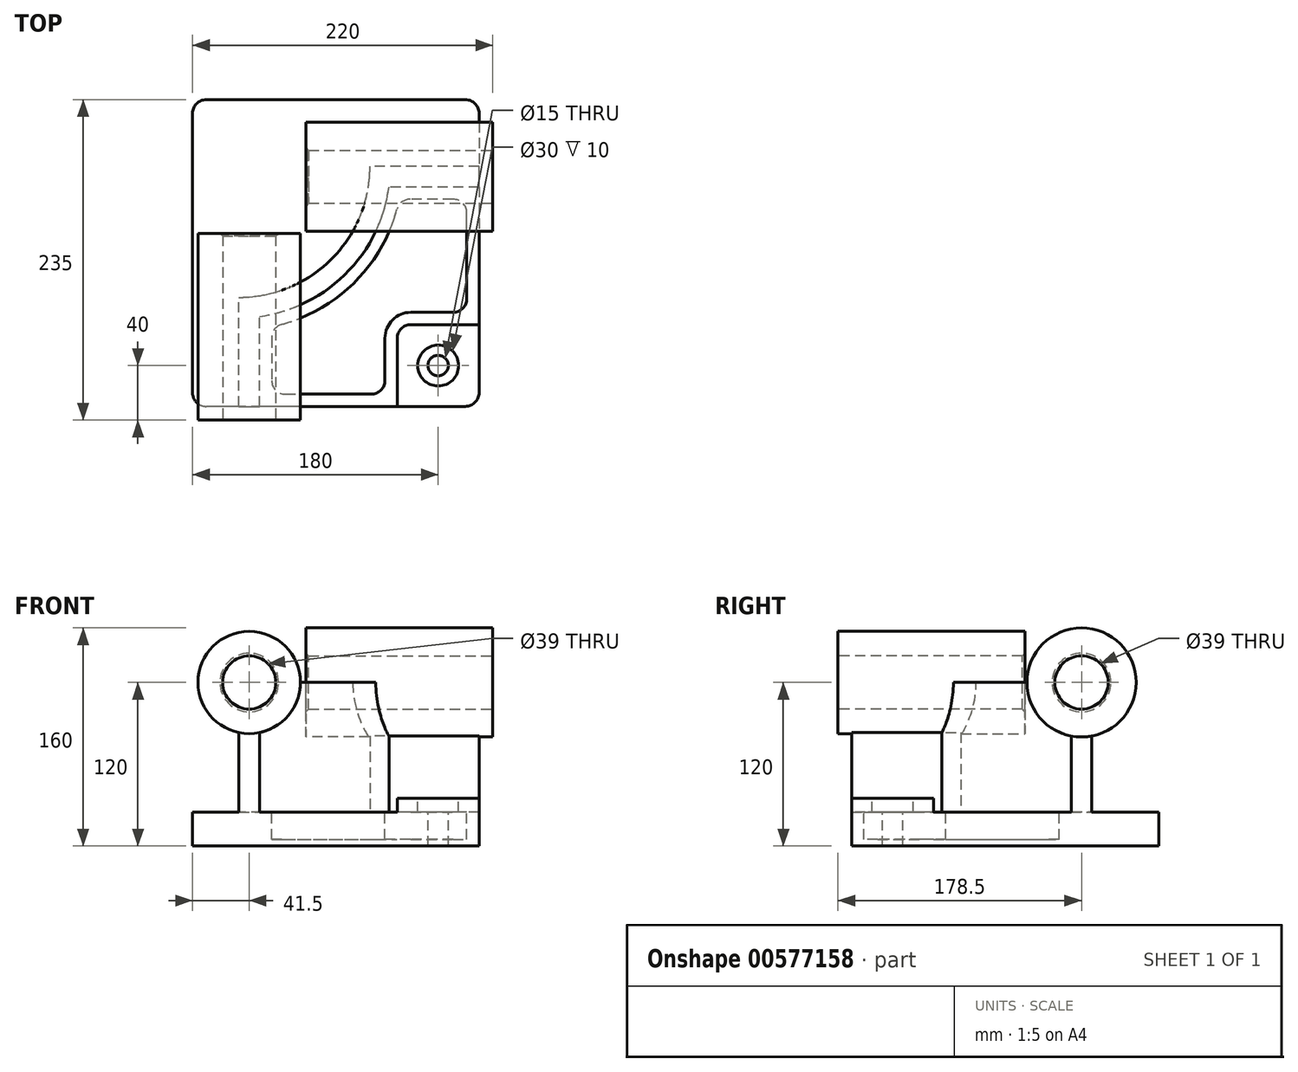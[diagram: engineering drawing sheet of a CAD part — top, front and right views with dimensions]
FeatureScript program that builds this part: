
annotation { "Feature Type Name" : "Feature", "Feature Type Description" : "" }
export const myFeature = defineFeature(function(context is Context, id is Id, definition is map)
    precondition{}
    {
        {
            var Q0;
            Q0=qCreatedBy(makeId("Top.planeOp"),FACE);
            var sketch = newSketch(context, id + "F0", { "sketchPlane" : qUnion([Q0])});
            skLineSegment(sketch, "E0.bottom", {"start": v(105, 112.5) * mm, "end": v(-105, 112.5) * mm});
            skLineSegment(sketch, "E0.top", {"start": v(105, -112.5) * mm, "end": v(-105, -112.5) * mm});
            skLineSegment(sketch, "E0.left", {"start": v(105, 112.5) * mm, "end": v(105, -112.5) * mm});
            skLineSegment(sketch, "E0.right", {"start": v(-105, 112.5) * mm, "end": v(-105, -112.5) * mm});
            skPoint(sketch, "E0.middle", {"position": v(0, 0) * mm});
            skSolve(sketch);
        }
        {
            var Q0;
            Q0=makeQuery(id+"F0.imprint","IMPRINT",FACE,{"disambiguationData":[TD([[makeQuery(id+"F0.imprint","IMPRINT",EDGE,{"derivedFrom":sQuery(id+"F0.wireOp",EDGE,"E0.bottom")}),1.0]])]});
            extrude(context, id + "F1", {"entities" : qUnion([Q0]), "depth" : 25 * mm, "offsetDistance" : 25 * mm});
        }
        {
            var Q0;
            Q0=makeQuery(id+"F1.opExtrude","CAP_FACE",FACE,{"disambiguationData":[OSD([sQuery(id+"F0.wireOp",EDGE,"E0.bottom"),sQuery(id+"F0.wireOp",EDGE,"E0.top"),sQuery(id+"F0.wireOp",EDGE,"E0.left"),sQuery(id+"F0.wireOp",EDGE,"E0.right")])],"isStart":false});
            var sketch = newSketch(context, id + "F2", { "sketchPlane" : qUnion([Q0])});
            skLineSegment(sketch, "E1", {"start": v(-71, -112.5) * mm, "end": v(-71, -32.5) * mm});
            skLineSegment(sketch, "E2", {"start": v(105, 63.5) * mm, "end": v(25, 63.5) * mm});
            skArc(sketch, "E3", {"start": v(-71, -32.5) * mm, "mid": v(-3.12, -4.38) * mm, "end": v(25, 63.5) * mm});
            skLineSegment(sketch, "E4", {"start": v(-71, 63.5) * mm, "end": v(25, 63.5) * mm, "construction": true});
            skLineSegment(sketch, "E5", {"start": v(-71, 63.5) * mm, "end": v(-71, -32.5) * mm, "construction": true});
            skLineSegment(sketch, "E6.0", {"start": v(-56, -112.5) * mm, "end": v(-56, -46.48) * mm});
            skArc(sketch, "E6.1", {"start": v(-56, -46.48) * mm, "mid": v(7.49, -14.99) * mm, "end": v(38.98, 48.5) * mm});
            skLineSegment(sketch, "E6.2", {"start": v(105, 48.5) * mm, "end": v(38.98, 48.5) * mm});
            skLineSegment(sketch, "E7.0", {"start": v(105, 112.5) * mm, "end": v(105, -112.5) * mm});
            skLineSegment(sketch, "E8.0", {"start": v(105, -112.5) * mm, "end": v(-105, -112.5) * mm});
            skSolve(sketch);
        }
        {
            var Q0;
            {var subQ2=sQuery(id+"F2.wireOp",EDGE,"E1");Q0=makeQuery(id+"F2.imprint","IMPRINT",FACE,{"disambiguationData":[TD([[makeQuery(id+"F2.imprint","IMPRINT",EDGE,{"derivedFrom":subQ2}),-1.0]])]});}
            extrude(context, id + "F3", {"entities" : qUnion([Q0]), "operationType" : NewBodyOperationType.ADD, "depth" : 95 * mm, "offsetDistance" : 25 * mm});
        }
        {
            var Q0;
            Q0=makeQuery(id+"F3.boolean.opBoolean","MERGE",FACE,{"derivedFrom":[makeQuery(id+"F1.opExtrude","SWEPT_FACE",FACE,{"disambiguationData":[OSD([sQuery(id+"F0.wireOp",EDGE,"E0.top")])]}),makeQuery(id+"F3.opExtrude","SWEPT_FACE",FACE,{"disambiguationData":[OSD([sQuery(id+"F2.wireOp",EDGE,"E8.0")])]})]});
            var sketch = newSketch(context, id + "F4", { "sketchPlane" : qUnion([Q0])});
            skCircle(sketch, "E9", {"center": v(-63.5, 120) * mm, "radius": 37.5 * mm});
            skSolve(sketch);
        }
        {
            var Q0;
            Q0 = qSketchRegion(id + "F4", true);
            extrude(context, id + "F5", {"entities" : qUnion([Q0]), "operationType" : NewBodyOperationType.ADD, "depth" : 10 * mm, "offsetDistance" : 25 * mm, "hasSecondDirection" : true, "secondDirectionOppositeDirection" : true, "secondDirectionDepth" : (137 - 10) * mm});
        }
        {
            var Q0;
            Q0=makeQuery(id+"F3.boolean.opBoolean","MERGE",FACE,{"derivedFrom":[makeQuery(id+"F1.opExtrude","SWEPT_FACE",FACE,{"disambiguationData":[OSD([sQuery(id+"F0.wireOp",EDGE,"E0.left")])]}),makeQuery(id+"F3.opExtrude","SWEPT_FACE",FACE,{"disambiguationData":[OSD([sQuery(id+"F2.wireOp",EDGE,"E7.0")])]})]});
            var sketch = newSketch(context, id + "F6", { "sketchPlane" : qUnion([Q0])});
            skCircle(sketch, "E10", {"center": v(56, 120) * mm, "radius": 40 * mm});
            skSolve(sketch);
        }
        {
            var Q0;
            Q0 = qSketchRegion(id + "F6", true);
            extrude(context, id + "F7", {"entities" : qUnion([Q0]), "operationType" : NewBodyOperationType.ADD, "depth" : 10 * mm, "offsetDistance" : 25 * mm, "hasSecondDirection" : true, "secondDirectionOppositeDirection" : true, "secondDirectionDepth" : (137 - 10) * mm});
        }
        {
            var Q0;
            {var subQ0=sQuery(id+"F0.wireOp",EDGE,"E0.left");var subQ1=sQuery(id+"F0.wireOp",EDGE,"E0.top");Q0=makeQuery(id+"F3.boolean.opBoolean","SPLIT",FACE,{"disambiguationData":[TD([makeQuery(id+"F3.opExtrude","SWEPT_FACE",FACE,{"disambiguationData":[OSD([sQuery(id+"F2.wireOp",EDGE,"E6.0")])]})])],"derivedFrom":makeQuery(id+"F1.opExtrude","CAP_FACE",FACE,{"disambiguationData":[OSD([sQuery(id+"F0.wireOp",EDGE,"E0.bottom"),subQ1,subQ0,sQuery(id+"F0.wireOp",EDGE,"E0.right")])],"isStart":false})});}
            var sketch = newSketch(context, id + "F8", { "sketchPlane" : qUnion([Q0])});
            skLineSegment(sketch, "E11.bottom", {"start": v(105, -112.5) * mm, "end": v(45, -112.5) * mm});
            skLineSegment(sketch, "E11.top", {"start": v(105, -52.5) * mm, "end": v(45, -52.5) * mm});
            skLineSegment(sketch, "E11.left", {"start": v(105, -112.5) * mm, "end": v(105, -52.5) * mm});
            skLineSegment(sketch, "E11.right", {"start": v(45, -112.5) * mm, "end": v(45, -52.5) * mm});
            skSolve(sketch);
        }
        {
            var Q0;
            Q0 = qSketchRegion(id + "F8", true);
            extrude(context, id + "F9", {"entities" : qUnion([Q0]), "operationType" : NewBodyOperationType.ADD, "depth" : (35 - 25) * mm, "offsetDistance" : 25 * mm});
        }
        {
            var Q0;
            Q0=makeQuery(id+"F9.opExtrude","SWEPT_EDGE",EDGE,{"disambiguationData":[OSD([sQuery(id+"F8.wireOp",EDGE,"E11.top"),sQuery(id+"F8.wireOp",EDGE,"E11.right")])]});
            fillet(context, id + "F10", {"entities" : qUnion([Q0]), "radius" : 10 * mm, "tangentPropagation" : true, "allowEdgeOverflow" : false});
        }
        {
            var Q0;
            {var subQ0=sQuery(id+"F0.wireOp",EDGE,"E0.left");var subQ1=sQuery(id+"F0.wireOp",EDGE,"E0.top");Q0=makeQuery(id+"F3.boolean.opBoolean","SPLIT",FACE,{"disambiguationData":[TD([makeQuery(id+"F3.opExtrude","SWEPT_FACE",FACE,{"disambiguationData":[OSD([sQuery(id+"F2.wireOp",EDGE,"E6.0")])]})])],"derivedFrom":makeQuery(id+"F1.opExtrude","CAP_FACE",FACE,{"disambiguationData":[OSD([sQuery(id+"F0.wireOp",EDGE,"E0.bottom"),subQ1,subQ0,sQuery(id+"F0.wireOp",EDGE,"E0.right")])],"isStart":false})});}
            var sketch = newSketch(context, id + "F11", { "sketchPlane" : qUnion([Q0])});
            skLineSegment(sketch, "E12.0", {"start": v(-47, -54.08) * mm, "end": v(-47, -103.5) * mm});
            skArc(sketch, "E12.1", {"start": v(46.58, 39.5) * mm, "mid": v(13.85, -21.35) * mm, "end": v(-47, -54.08) * mm});
            skLineSegment(sketch, "E12.2", {"start": v(-47, -103.5) * mm, "end": v(36, -103.5) * mm});
            skLineSegment(sketch, "E12.3", {"start": v(96, 39.5) * mm, "end": v(46.58, 39.5) * mm});
            skLineSegment(sketch, "E12.4", {"start": v(36, -103.5) * mm, "end": v(36, -62.5) * mm});
            skArc(sketch, "E12.5", {"start": v(36, -62.5) * mm, "mid": v(41.56, -49.06) * mm, "end": v(55, -43.5) * mm});
            skLineSegment(sketch, "E12.6", {"start": v(55, -43.5) * mm, "end": v(96, -43.5) * mm});
            skLineSegment(sketch, "E12.7", {"start": v(96, -43.5) * mm, "end": v(96, 39.5) * mm});
            skSolve(sketch);
        }
        {
            var Q0;
            Q0=makeQuery(id+"F11.imprint","IMPRINT",FACE,{"disambiguationData":[TD([[makeQuery(id+"F11.imprint","IMPRINT",EDGE,{"derivedFrom":sQuery(id+"F11.wireOp",EDGE,"E12.0")}),1.0]])]});
            extrude(context, id + "F12", {"entities" : qUnion([Q0]), "operationType" : NewBodyOperationType.REMOVE, "oppositeDirection" : true, "depth" : (25 - 5) * mm, "offsetDistance" : 25 * mm});
        }
        {
            var Q0;
            Q0=makeQuery(id+"F9.opExtrude","CAP_FACE",FACE,{"disambiguationData":[OSD([sQuery(id+"F8.wireOp",EDGE,"E11.bottom"),sQuery(id+"F8.wireOp",EDGE,"E11.top"),sQuery(id+"F8.wireOp",EDGE,"E11.left"),sQuery(id+"F8.wireOp",EDGE,"E11.right")])],"isStart":false});
            var sketch = newSketch(context, id + "F13", { "sketchPlane" : qUnion([Q0])});
            skCircle(sketch, "E13", {"center": v(75, -82.5) * mm, "radius": 15 * mm});
            skSolve(sketch);
        }
        {
            var Q0;
            Q0=sQuery(id+"F13.wireOp",VERTEX,"E13.center");
            var Q1;
            Q1=makeQuery(id+"F1.opExtrude","SWEPT_BODY",BODY,{"disambiguationData":[OSD([sQuery(id+"F0.wireOp",EDGE,"E0.bottom"),sQuery(id+"F0.wireOp",EDGE,"E0.top"),sQuery(id+"F0.wireOp",EDGE,"E0.left"),sQuery(id+"F0.wireOp",EDGE,"E0.right")])]});
            hole(context, id + "F14", {"style" : HoleStyle.C_BORE, "endStyle" : HoleEndStyle.THROUGH, "holeDiameter" : 15 * mm, "cBoreDiameter" : 30 * mm, "cBoreDepth" : 10 * mm, "isTappedThrough" : true, "tappedDepth" : 12 * mm, "tapClearance" : 3, "locations" : qUnion([Q0]), "scope" : qUnion([Q1])});
        }
        {
            var Q0;
            Q0=makeQuery(id+"F12.boolean.opBoolean","COPY",EDGE,{"derivedFrom":makeQuery(id+"F12.opExtrude","SWEPT_EDGE",EDGE,{"disambiguationData":[OSD([sQuery(id+"F11.wireOp",EDGE,"E12.0"),sQuery(id+"F11.wireOp",EDGE,"E12.1")])]})});
            var Q1;
            Q1=makeQuery(id+"F12.boolean.opBoolean","COPY",EDGE,{"derivedFrom":makeQuery(id+"F12.opExtrude","SWEPT_EDGE",EDGE,{"disambiguationData":[OSD([sQuery(id+"F11.wireOp",EDGE,"E12.1"),sQuery(id+"F11.wireOp",EDGE,"E12.3")])]})});
            var Q2;
            Q2=makeQuery(id+"F12.boolean.opBoolean","COPY",EDGE,{"derivedFrom":makeQuery(id+"F12.opExtrude","SWEPT_EDGE",EDGE,{"disambiguationData":[OSD([sQuery(id+"F11.wireOp",EDGE,"E12.0"),sQuery(id+"F11.wireOp",EDGE,"E12.2")])]})});
            var Q3;
            Q3=makeQuery(id+"F12.boolean.opBoolean","COPY",EDGE,{"derivedFrom":makeQuery(id+"F12.opExtrude","SWEPT_EDGE",EDGE,{"disambiguationData":[OSD([sQuery(id+"F11.wireOp",EDGE,"E12.3"),sQuery(id+"F11.wireOp",EDGE,"E12.7")])]})});
            var Q4;
            Q4=makeQuery(id+"F12.boolean.opBoolean","COPY",EDGE,{"derivedFrom":makeQuery(id+"F12.opExtrude","SWEPT_EDGE",EDGE,{"disambiguationData":[OSD([sQuery(id+"F11.wireOp",EDGE,"E12.2"),sQuery(id+"F11.wireOp",EDGE,"E12.4")])]})});
            var Q5;
            Q5=makeQuery(id+"F12.boolean.opBoolean","COPY",EDGE,{"derivedFrom":makeQuery(id+"F12.opExtrude","SWEPT_EDGE",EDGE,{"disambiguationData":[OSD([sQuery(id+"F11.wireOp",EDGE,"E12.6"),sQuery(id+"F11.wireOp",EDGE,"E12.7")])]})});
            fillet(context, id + "F15", {"entities" : qUnion([Q0, Q1, Q2, Q3, Q4, Q5]), "radius" : 10 * mm, "tangentPropagation" : true, "allowEdgeOverflow" : false});
        }
        {
            var Q0;
            Q0=makeQuery(id+"F5.opExtrude","CAP_FACE",FACE,{"disambiguationData":[OSD([sQuery(id+"F4.wireOp",EDGE,"E9")])],"isStart":false});
            var sketch = newSketch(context, id + "F16", { "sketchPlane" : qUnion([Q0])});
            skCircle(sketch, "E14", {"center": v(-63.5, 120) * mm, "radius": 19.5 * mm});
            skSolve(sketch);
        }
        {
            var Q0;
            Q0 = qSketchRegion(id + "F16", true);
            extrude(context, id + "F17", {"entities" : qUnion([Q0]), "operationType" : NewBodyOperationType.REMOVE, "endBound" : BoundingType.THROUGH_ALL, "oppositeDirection" : true, "depth" : 25 * mm, "offsetDistance" : 25 * mm});
        }
        {
            var Q0;
            Q0=makeQuery(id+"F7.opExtrude","CAP_FACE",FACE,{"disambiguationData":[OSD([sQuery(id+"F6.wireOp",EDGE,"E10")])],"isStart":false});
            var sketch = newSketch(context, id + "F18", { "sketchPlane" : qUnion([Q0])});
            skCircle(sketch, "E15", {"center": v(56, 120) * mm, "radius": 19.5 * mm});
            skSolve(sketch);
        }
        {
            var Q0;
            Q0 = qSketchRegion(id + "F18", true);
            extrude(context, id + "F19", {"entities" : qUnion([Q0]), "operationType" : NewBodyOperationType.REMOVE, "endBound" : BoundingType.THROUGH_ALL, "oppositeDirection" : true, "depth" : 25 * mm, "offsetDistance" : 25 * mm});
        }
        {
            var Q0;
            Q0=makeQuery(id+"F17.boolean.opBoolean","COPY",EDGE,{"derivedFrom":makeQuery(id+"F17.opExtrude","CAP_EDGE",EDGE,{"disambiguationData":[OSD([sQuery(id+"F16.wireOp",EDGE,"E14")])],"isStart":true})});
            var Q1;
            Q1=makeQuery(id+"F19.boolean.opBoolean","COPY",EDGE,{"derivedFrom":makeQuery(id+"F19.opExtrude","CAP_EDGE",EDGE,{"disambiguationData":[OSD([sQuery(id+"F18.wireOp",EDGE,"E15")])],"isStart":true})});
            var Q2;
            Q2=makeQuery(id+"F19.boolean.opBoolean","INTERSECT",EDGE,{"derivedFrom":[makeQuery(id+"F7.opExtrude","CAP_FACE",FACE,{"disambiguationData":[OSD([sQuery(id+"F6.wireOp",EDGE,"E10")])],"isStart":true}),makeQuery(id+"F19.opExtrude","SWEPT_FACE",FACE,{"disambiguationData":[OSD([sQuery(id+"F18.wireOp",EDGE,"E15")])]})]});
            var Q3;
            Q3=makeQuery(id+"F17.boolean.opBoolean","INTERSECT",EDGE,{"derivedFrom":[makeQuery(id+"F5.opExtrude","CAP_FACE",FACE,{"disambiguationData":[OSD([sQuery(id+"F4.wireOp",EDGE,"E9")])],"isStart":true}),makeQuery(id+"F17.opExtrude","SWEPT_FACE",FACE,{"disambiguationData":[OSD([sQuery(id+"F16.wireOp",EDGE,"E14")])]})]});
            chamfer(context, id + "F20", {"entities" : qUnion([Q0, Q1, Q2, Q3]), "width" : 2 * mm, "tangentPropagation" : true});
        }
        {
            var Q0;
            Q0=makeQuery(id+"F1.opExtrude","SWEPT_EDGE",EDGE,{"disambiguationData":[OSD([sQuery(id+"F0.wireOp",EDGE,"E0.top"),sQuery(id+"F0.wireOp",EDGE,"E0.right")])]});
            var Q1;
            Q1=makeQuery(id+"F9.boolean.opBoolean","MERGE",EDGE,{"derivedFrom":[makeQuery(id+"F1.opExtrude","SWEPT_EDGE",EDGE,{"disambiguationData":[OSD([sQuery(id+"F0.wireOp",EDGE,"E0.top"),sQuery(id+"F0.wireOp",EDGE,"E0.left")])]}),makeQuery(id+"F9.opExtrude","SWEPT_EDGE",EDGE,{"disambiguationData":[OSD([sQuery(id+"F8.wireOp",EDGE,"E11.bottom"),sQuery(id+"F8.wireOp",EDGE,"E11.left")])]})]});
            var Q2;
            Q2=makeQuery(id+"F1.opExtrude","SWEPT_EDGE",EDGE,{"disambiguationData":[OSD([sQuery(id+"F0.wireOp",EDGE,"E0.bottom"),sQuery(id+"F0.wireOp",EDGE,"E0.left")])]});
            var Q3;
            Q3=makeQuery(id+"F1.opExtrude","SWEPT_EDGE",EDGE,{"disambiguationData":[OSD([sQuery(id+"F0.wireOp",EDGE,"E0.bottom"),sQuery(id+"F0.wireOp",EDGE,"E0.right")])]});
            fillet(context, id + "F21", {"entities" : qUnion([Q0, Q1, Q2, Q3]), "radius" : 10 * mm, "tangentPropagation" : true, "allowEdgeOverflow" : false});
        }
    });
